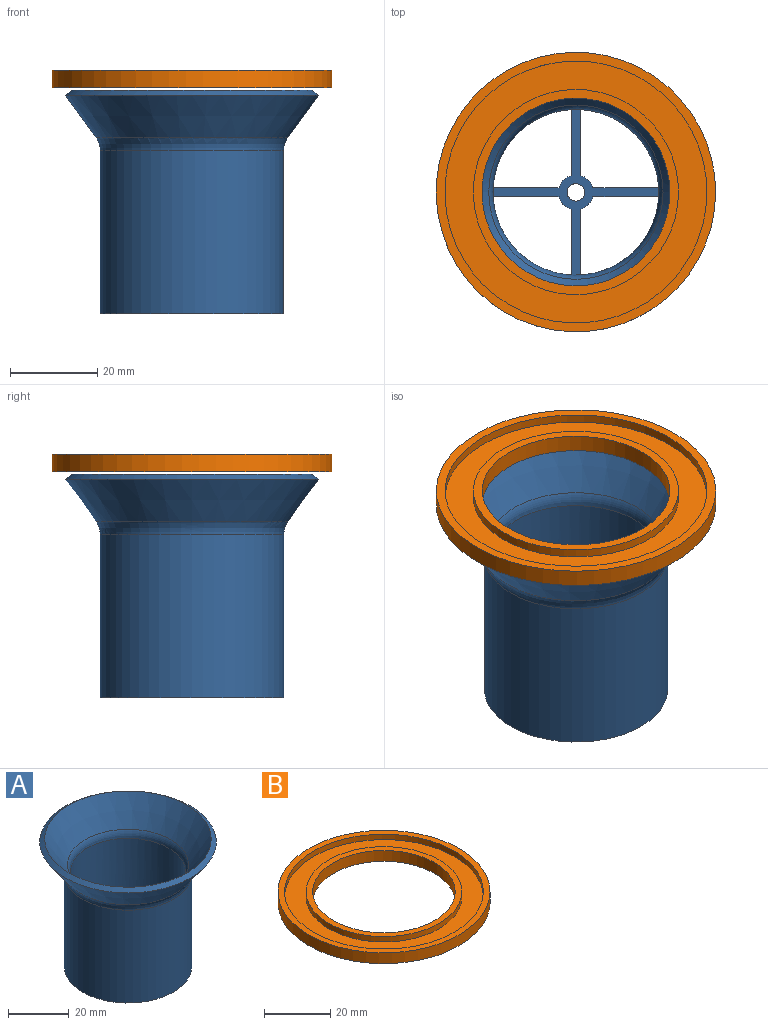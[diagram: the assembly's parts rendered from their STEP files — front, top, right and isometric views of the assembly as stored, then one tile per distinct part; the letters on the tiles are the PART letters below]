
ASSEMBLY  parts=2 mates=1
PART A: 22 faces, bbox 58x58x51.2 mm
  f0: plane 38x38mm, normal (0,0,1), area 158mm2, adj f1,f2,f4,f5,f6,f7,f8,f9
  f1: plane 15.1x13mm, normal (1,0,0), area 196.3mm2, adj f0,f3,f8,f19
  f2: plane 15.1x13mm, normal (-1,0,0), area 196.3mm2, adj f0,f3,f4,f19
  f3: plane 42x42mm, normal (0,0,-1), area 409.3mm2, adj f1,f2,f4,f5,f6,f7,f8,f9
  f4: cylinder r=4mm len=13mm, axis (0,0,-1), area 55.4mm2, adj f0,f2,f3,f5
  f5: plane 15.1x13mm, normal (0,1,0), area 196.3mm2, adj f0,f3,f4,f19
  f6: plane 15.1x13mm, normal (0,-1,0), area 196.3mm2, adj f0,f3,f7,f19
  f7: cylinder r=4mm len=13mm, axis (0,0,-1), area 55.4mm2, adj f0,f3,f6,f13
  f8: cylinder r=4mm len=13mm, axis (0,0,-1), area 55.4mm2, adj f0,f1,f3,f12
  f9: cylinder r=2mm len=13mm, axis (0,0,-1), area 163.4mm2, adj f0,f3
  f10: cylinder r=4mm len=13mm, axis (0,0,-1), area 55.4mm2, adj f0,f3,f11,f14
  f11: plane 15.1x13mm, normal (0,-1,0), area 196.3mm2, adj f0,f3,f10,f19
  f12: plane 15.1x13mm, normal (0,1,0), area 196.3mm2, adj f0,f3,f8,f19
  f13: plane 15.1x13mm, normal (-1,0,0), area 196.3mm2, adj f0,f3,f7,f19
  f14: plane 15.1x13mm, normal (1,0,0), area 196.3mm2, adj f0,f3,f10,f19
  f15: cylinder r=21mm len=42mm, axis (0,0,-1), area 4931.4mm2, adj f3,f20
  f16: cone r=21mm half-angle=36deg, axis (0,0,1), area 1917.1mm2, adj f17,f20
  f17: cone r=29mm half-angle=54deg, axis (0,0,-1), area 354.3mm2, adj f16,f18
  f18: cone r=19mm half-angle=36deg, axis (0,0,1), area 1877.7mm2, adj f17,f21
  f19: cylinder r=19mm len=38.02mm, axis (0,0,-1), area 4435.3mm2, adj f0,f1,f2,f3,f5,f6,f11,f12
  f20: torus R=26mm, axis (0,0,-1), area 421.2mm2, adj f15,f16
  f21: torus R=24mm, axis (0,0,1), area 381.7mm2, adj f18,f19
PART B: 8 faces, bbox 64x64x4 mm
  f0: cylinder r=21.5mm len=43mm, axis (0,0,-1), area 540.4mm2, adj f1,f7
  f1: plane 64x64mm, normal (0,0,-1), area 1764.8mm2, adj f0,f2
  f2: cylinder r=32mm len=64mm, axis (0,0,-1), area 804.2mm2, adj f1,f3
  f3: plane 64x64mm, normal (0,0,1), area 389.6mm2, adj f2,f4
  f4: cylinder r=30mm len=60mm, axis (0,0,-1), area 377mm2, adj f3,f5
  f5: plane 60x60mm, normal (0,0,1), area 1092.5mm2, adj f4,f6
  f6: cylinder r=23.5mm len=47mm, axis (0,0,-1), area 295.3mm2, adj f5,f7
  f7: plane 47x47mm, normal (0,0,1), area 282.7mm2, adj f0,f6
PLACE A at identity fixed
PLACE B rot(axis=(0,0,1),59.4deg) t=(0,0,51.7)mm
MATE cylindrical B.f0 <-> A.f15  axis (0,0,-1) through (0,0,53.7)mm
